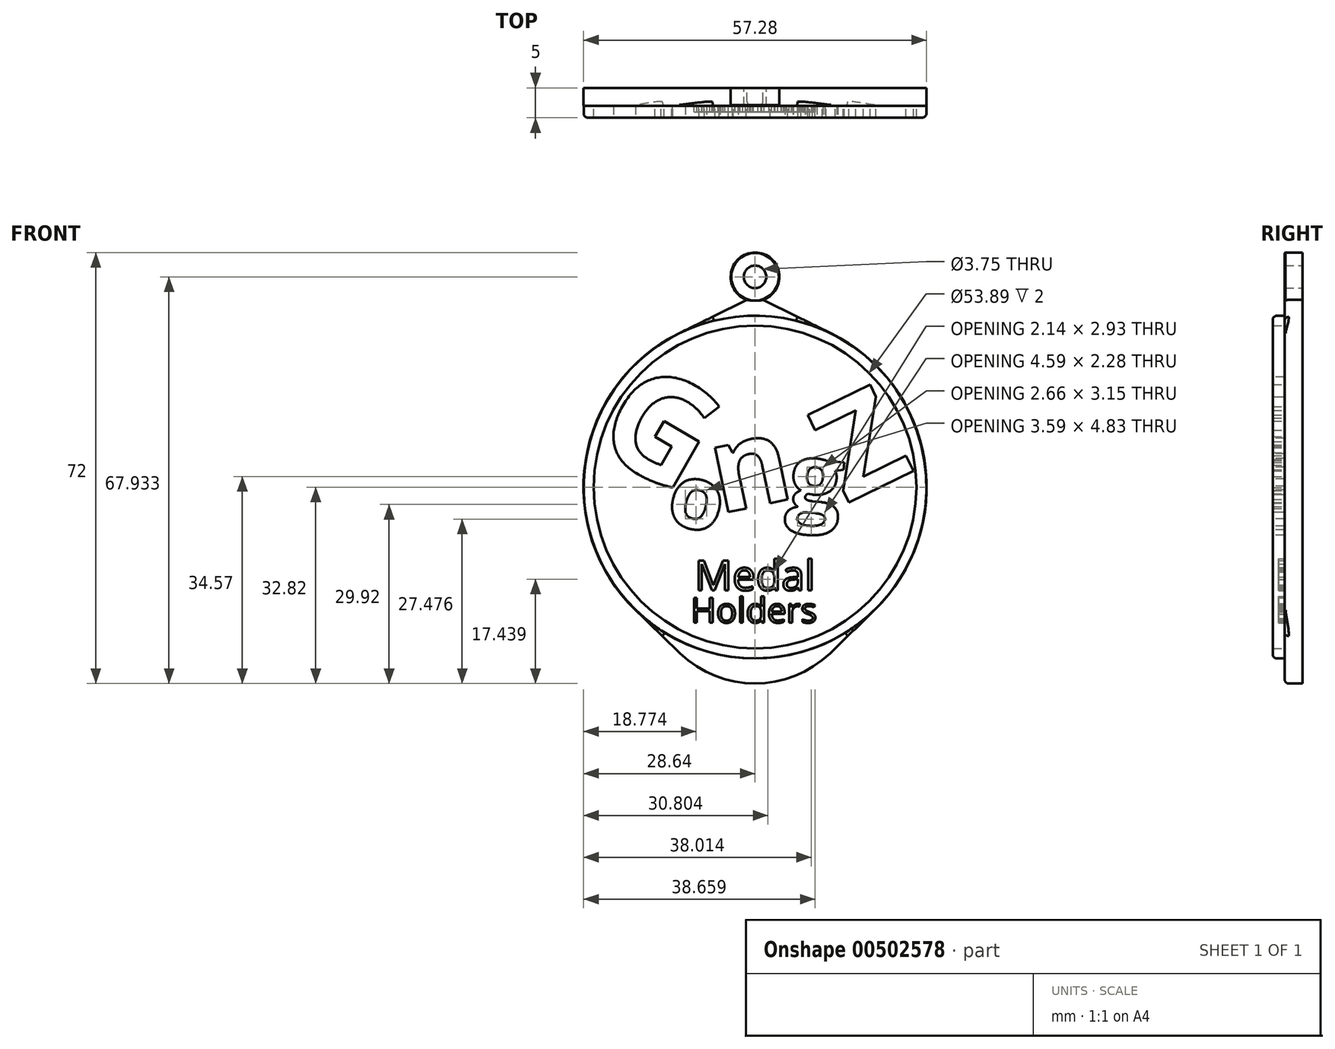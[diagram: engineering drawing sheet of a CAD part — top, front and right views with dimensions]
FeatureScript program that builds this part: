
annotation { "Feature Type Name" : "Feature", "Feature Type Description" : "" }
export const myFeature = defineFeature(function(context is Context, id is Id, definition is map)
    precondition{}
    {
        {
            var Q0;
            Q0=qCreatedBy(makeId("Front.planeOp"),FACE);
            var sketch = newSketch(context, id + "F0", { "sketchPlane" : qUnion([Q0])});
            skArc(sketch, "E0", {"start": v(19.93, -20.57) * mm, "mid": v(28.3, 4.45) * mm, "end": v(12.66, 25.7) * mm});
            skLineSegment(sketch, "E1", {"start": v(-12.53, -27.75) * mm, "end": v(-19.93, -20.57) * mm});
            skLineSegment(sketch, "E2", {"start": v(12.53, -27.75) * mm, "end": v(19.93, -20.57) * mm});
            skPoint(sketch, "E3.visualSharp", {"position": v(0, -39.89) * mm});
            skArc(sketch, "E3.filletArc", {"start": v(-12.53, -27.75) * mm, "mid": v(0, -32.82) * mm, "end": v(12.53, -27.75) * mm});
            skLineSegment(sketch, "E4", {"start": v(-1.34, 31.27) * mm, "end": v(-12.66, 25.7) * mm});
            skLineSegment(sketch, "E5", {"start": v(-12.66, 25.7) * mm, "end": v(-1.34, 31.27) * mm});
            skLineSegment(sketch, "E6", {"start": v(1.34, 31.27) * mm, "end": v(12.66, 25.7) * mm});
            skArc(sketch, "E7.trimOffspring", {"start": v(-12.66, 25.7) * mm, "mid": v(-28.3, 4.45) * mm, "end": v(-19.93, -20.57) * mm});
            skCircle(sketch, "E8", {"center": v(0, 35.11) * mm, "radius": 4.07 * mm});
            skCircle(sketch, "E9", {"center": v(0, 35.11) * mm, "radius": 1.87 * mm});
            skPoint(sketch, "E10.orphan", {"position": v(0, 31.93) * mm});
            skSolve(sketch);
        }
        {
            var Q0;
            Q0 = qSketchRegion(id + "F0", true);
            extrude(context, id + "F1", {"entities" : qUnion([Q0]), "depth" : 3 * mm, "offsetDistance" : 25 * mm});
        }
        {
            var Q0;
            Q0=makeQuery(id+"F1.opExtrude","CAP_FACE",FACE,{"disambiguationData":[OSD([sQuery(id+"F0.wireOp",EDGE,"E0"),sQuery(id+"F0.wireOp",EDGE,"E1"),sQuery(id+"F0.wireOp",EDGE,"E2"),sQuery(id+"F0.wireOp",EDGE,"E3.filletArc"),sQuery(id+"F0.wireOp",EDGE,"E5"),sQuery(id+"F0.wireOp",EDGE,"E6"),sQuery(id+"F0.wireOp",EDGE,"E7.trimOffspring"),sQuery(id+"F0.wireOp",EDGE,"E8"),sQuery(id+"F0.wireOp",EDGE,"E9")])],"isStart":false});
            var sketch = newSketch(context, id + "F2", { "sketchPlane" : qUnion([Q0])});
            skCircle(sketch, "E11", {"center": v(0, 0) * mm, "radius": 28.62 * mm});
            skCircle(sketch, "E12", {"center": v(0, 0) * mm, "radius": 26.95 * mm});
            skSolve(sketch);
        }
        {
            var Q0;
            Q0 = qSketchRegion(id + "F2", true);
            extrude(context, id + "F3", {"entities" : qUnion([Q0]), "operationType" : NewBodyOperationType.ADD, "depth" : 2 * mm, "offsetDistance" : 25 * mm});
        }
        {
            var Q0;
            Q0=makeQuery(id+"F1.opExtrude","CAP_EDGE",EDGE,{"disambiguationData":[OSD([sQuery(id+"F0.wireOp",EDGE,"E3.filletArc")])],"isStart":false});
            var Q1;
            Q1=makeQuery(id+"F1.opExtrude","CAP_EDGE",EDGE,{"disambiguationData":[OSD([sQuery(id+"F0.wireOp",EDGE,"E2")])],"isStart":false});
            var Q2;
            Q2=makeQuery(id+"F1.opExtrude","CAP_EDGE",EDGE,{"disambiguationData":[OSD([sQuery(id+"F0.wireOp",EDGE,"E1")])],"isStart":false});
            var Q3;
            Q3=makeQuery(id+"F3.opExtrude","CAP_EDGE",EDGE,{"disambiguationData":[OSD([sQuery(id+"F2.wireOp",EDGE,"E11")])],"isStart":false});
            fillet(context, id + "F4", {"entities" : qUnion([Q0, Q1, Q2, Q3]), "radius" : .7 * mm, "tangentPropagation" : true, "allowEdgeOverflow" : false});
        }
        {
            var Q0;
            Q0=makeQuery(id+"F1.opExtrude","CAP_EDGE",EDGE,{"disambiguationData":[OSD([sQuery(id+"F0.wireOp",EDGE,"E8")])],"isStart":false});
            chamfer(context, id + "F5", {"entities" : qUnion([Q0]), "width" : .1 * mm, "tangentPropagation" : true});
        }
        {
            var Q0;
            Q0=makeQuery(id+"F3.boolean.opBoolean","SPLIT",FACE,{"disambiguationData":[TD([makeQuery(id+"F3.opExtrude","SWEPT_FACE",FACE,{"disambiguationData":[OSD([sQuery(id+"F2.wireOp",EDGE,"E12")])]})])],"derivedFrom":makeQuery(id+"F1.opExtrude","CAP_FACE",FACE,{"disambiguationData":[OSD([sQuery(id+"F0.wireOp",EDGE,"E0"),sQuery(id+"F0.wireOp",EDGE,"E1"),sQuery(id+"F0.wireOp",EDGE,"E2"),sQuery(id+"F0.wireOp",EDGE,"E3.filletArc"),sQuery(id+"F0.wireOp",EDGE,"E5"),sQuery(id+"F0.wireOp",EDGE,"E6"),sQuery(id+"F0.wireOp",EDGE,"E7.trimOffspring"),sQuery(id+"F0.wireOp",EDGE,"E8"),sQuery(id+"F0.wireOp",EDGE,"E9")])],"isStart":false})});
            var sketch = newSketch(context, id + "F6", { "sketchPlane" : qUnion([Q0])});
            skText(sketch, "E13", { "text": "G", "fontName": "OpenSans-Bold.ttf"});
            const initialGuessF6  = {"E13": [-0.01287, -0.00489, 1, 0, 0.01727]};
            skSetInitialGuess(sketch, initialGuessF6);
            skSolve(sketch);
        }
        {
            var Q0;
            Q0 = qSketchRegion(id + "F6", true);
            extrude(context, id + "F7", {"entities" : qUnion([Q0]), "depth" : 2 * mm, "offsetDistance" : 25 * mm});
        }
        {
            var Q0;
            Q0=makeQuery(id+"F7.opExtrude","SWEPT_BODY",BODY,{"disambiguationData":[OSD([sQuery(id+"F6.wireOp",EDGE,"E13.sketch_text.stroke-0"),sQuery(id+"F6.wireOp",EDGE,"E13.sketch_text.stroke-1"),sQuery(id+"F6.wireOp",EDGE,"E13.sketch_text.stroke-2"),sQuery(id+"F6.wireOp",EDGE,"E13.sketch_text.stroke-3"),sQuery(id+"F6.wireOp",EDGE,"E13.sketch_text.stroke-4"),sQuery(id+"F6.wireOp",EDGE,"E13.sketch_text.stroke-5"),sQuery(id+"F6.wireOp",EDGE,"E13.sketch_text.stroke-6"),sQuery(id+"F6.wireOp",EDGE,"E13.sketch_text.stroke-7"),sQuery(id+"F6.wireOp",EDGE,"E13.sketch_text.stroke-8"),sQuery(id+"F6.wireOp",EDGE,"E13.sketch_text.stroke-9"),sQuery(id+"F6.wireOp",EDGE,"E13.sketch_text.stroke-10"),sQuery(id+"F6.wireOp",EDGE,"E13.sketch_text.stroke-11"),sQuery(id+"F6.wireOp",EDGE,"E13.sketch_text.stroke-12"),sQuery(id+"F6.wireOp",EDGE,"E13.sketch_text.stroke-13"),sQuery(id+"F6.wireOp",EDGE,"E13.sketch_text.stroke-14"),sQuery(id+"F6.wireOp",EDGE,"E13.sketch_text.stroke-15"),sQuery(id+"F6.wireOp",EDGE,"E13.sketch_text.stroke-16"),sQuery(id+"F6.wireOp",EDGE,"E13.sketch_text.stroke-17"),sQuery(id+"F6.wireOp",EDGE,"E13.sketch_text.stroke-18")])]});
            transform(context, id + "F8", {"entities" : qUnion([Q0]), "transformType" : TransformType.TRANSLATION_3D, "dx" : -11.7 * mm, "dy" : 0 * mm, "dz" : 4.6 * mm, "makeCopy" : false});
        }
        {
            var Q0;
            Q0=makeQuery(id+"F7.opExtrude","SWEPT_BODY",BODY,{"disambiguationData":[OSD([sQuery(id+"F6.wireOp",EDGE,"E13.sketch_text.stroke-0"),sQuery(id+"F6.wireOp",EDGE,"E13.sketch_text.stroke-1"),sQuery(id+"F6.wireOp",EDGE,"E13.sketch_text.stroke-2"),sQuery(id+"F6.wireOp",EDGE,"E13.sketch_text.stroke-3"),sQuery(id+"F6.wireOp",EDGE,"E13.sketch_text.stroke-4"),sQuery(id+"F6.wireOp",EDGE,"E13.sketch_text.stroke-5"),sQuery(id+"F6.wireOp",EDGE,"E13.sketch_text.stroke-6"),sQuery(id+"F6.wireOp",EDGE,"E13.sketch_text.stroke-7"),sQuery(id+"F6.wireOp",EDGE,"E13.sketch_text.stroke-8"),sQuery(id+"F6.wireOp",EDGE,"E13.sketch_text.stroke-9"),sQuery(id+"F6.wireOp",EDGE,"E13.sketch_text.stroke-10"),sQuery(id+"F6.wireOp",EDGE,"E13.sketch_text.stroke-11"),sQuery(id+"F6.wireOp",EDGE,"E13.sketch_text.stroke-12"),sQuery(id+"F6.wireOp",EDGE,"E13.sketch_text.stroke-13"),sQuery(id+"F6.wireOp",EDGE,"E13.sketch_text.stroke-14"),sQuery(id+"F6.wireOp",EDGE,"E13.sketch_text.stroke-15"),sQuery(id+"F6.wireOp",EDGE,"E13.sketch_text.stroke-16"),sQuery(id+"F6.wireOp",EDGE,"E13.sketch_text.stroke-17"),sQuery(id+"F6.wireOp",EDGE,"E13.sketch_text.stroke-18")])]});
            var Q1;
            Q1=makeQuery(id+"F7.opExtrude","SWEPT_EDGE",EDGE,{"disambiguationData":[OSD([sQuery(id+"F6.wireOp",EDGE,"E13.sketch_text.stroke-17"),sQuery(id+"F6.wireOp",EDGE,"E13.sketch_text.stroke-18")])]});
            transform(context, id + "F9", {"entities" : qUnion([Q0]), "transformType" : TransformType.ROTATION, "transformAxis" : qUnion([Q1]), "angle" : 30 * degree, "makeCopy" : false});
        }
        {
            var Q0;
            Q0=makeQuery(id+"F7.opExtrude","SWEPT_BODY",BODY,{"disambiguationData":[OSD([sQuery(id+"F6.wireOp",EDGE,"E13.sketch_text.stroke-0"),sQuery(id+"F6.wireOp",EDGE,"E13.sketch_text.stroke-1"),sQuery(id+"F6.wireOp",EDGE,"E13.sketch_text.stroke-2"),sQuery(id+"F6.wireOp",EDGE,"E13.sketch_text.stroke-3"),sQuery(id+"F6.wireOp",EDGE,"E13.sketch_text.stroke-4"),sQuery(id+"F6.wireOp",EDGE,"E13.sketch_text.stroke-5"),sQuery(id+"F6.wireOp",EDGE,"E13.sketch_text.stroke-6"),sQuery(id+"F6.wireOp",EDGE,"E13.sketch_text.stroke-7"),sQuery(id+"F6.wireOp",EDGE,"E13.sketch_text.stroke-8"),sQuery(id+"F6.wireOp",EDGE,"E13.sketch_text.stroke-9"),sQuery(id+"F6.wireOp",EDGE,"E13.sketch_text.stroke-10"),sQuery(id+"F6.wireOp",EDGE,"E13.sketch_text.stroke-11"),sQuery(id+"F6.wireOp",EDGE,"E13.sketch_text.stroke-12"),sQuery(id+"F6.wireOp",EDGE,"E13.sketch_text.stroke-13"),sQuery(id+"F6.wireOp",EDGE,"E13.sketch_text.stroke-14"),sQuery(id+"F6.wireOp",EDGE,"E13.sketch_text.stroke-15"),sQuery(id+"F6.wireOp",EDGE,"E13.sketch_text.stroke-16"),sQuery(id+"F6.wireOp",EDGE,"E13.sketch_text.stroke-17"),sQuery(id+"F6.wireOp",EDGE,"E13.sketch_text.stroke-18")])]});
            transform(context, id + "F10", {"entities" : qUnion([Q0]), "transformType" : TransformType.TRANSLATION_3D, "dx" : -0.8 * mm, "dy" : 0 * mm, "dz" : 2.1 * mm, "makeCopy" : false});
        }
        {
            var Q0;
            Q0=makeQuery(id+"F3.boolean.opBoolean","SPLIT",FACE,{"disambiguationData":[TD([makeQuery(id+"F3.opExtrude","SWEPT_FACE",FACE,{"disambiguationData":[OSD([sQuery(id+"F2.wireOp",EDGE,"E12")])]})])],"derivedFrom":makeQuery(id+"F1.opExtrude","CAP_FACE",FACE,{"disambiguationData":[OSD([sQuery(id+"F0.wireOp",EDGE,"E0"),sQuery(id+"F0.wireOp",EDGE,"E1"),sQuery(id+"F0.wireOp",EDGE,"E2"),sQuery(id+"F0.wireOp",EDGE,"E3.filletArc"),sQuery(id+"F0.wireOp",EDGE,"E5"),sQuery(id+"F0.wireOp",EDGE,"E6"),sQuery(id+"F0.wireOp",EDGE,"E7.trimOffspring"),sQuery(id+"F0.wireOp",EDGE,"E8"),sQuery(id+"F0.wireOp",EDGE,"E9")])],"isStart":false})});
            var sketch = newSketch(context, id + "F11", { "sketchPlane" : qUnion([Q0])});
            skText(sketch, "E14", { "text": "o", "fontName": "OpenSans-Bold.ttf"});
            const initialGuessF11  = {"E14": [-0.00372, -0.00779, 1, 0, 0.0107]};
            skSetInitialGuess(sketch, initialGuessF11);
            skSolve(sketch);
        }
        {
            var Q0;
            Q0 = qSketchRegion(id + "F11", true);
            extrude(context, id + "F12", {"entities" : qUnion([Q0]), "depth" : 2 * mm, "offsetDistance" : 25 * mm});
        }
        {
            var Q0;
            Q0=makeQuery(id+"F12.opExtrude","SWEPT_BODY",BODY,{"disambiguationData":[OSD([sQuery(id+"F11.wireOp",EDGE,"E14.sketch_text.stroke-0"),sQuery(id+"F11.wireOp",EDGE,"E14.sketch_text.stroke-1"),sQuery(id+"F11.wireOp",EDGE,"E14.sketch_text.stroke-2"),sQuery(id+"F11.wireOp",EDGE,"E14.sketch_text.stroke-3"),sQuery(id+"F11.wireOp",EDGE,"E14.sketch_text.stroke-4"),sQuery(id+"F11.wireOp",EDGE,"E14.sketch_text.stroke-5"),sQuery(id+"F11.wireOp",EDGE,"E14.sketch_text.stroke-6"),sQuery(id+"F11.wireOp",EDGE,"E14.sketch_text.stroke-7"),sQuery(id+"F11.wireOp",EDGE,"E14.sketch_text.stroke-8"),sQuery(id+"F11.wireOp",EDGE,"E14.sketch_text.stroke-9"),sQuery(id+"F11.wireOp",EDGE,"E14.sketch_text.stroke-10"),sQuery(id+"F11.wireOp",EDGE,"E14.sketch_text.stroke-11"),sQuery(id+"F11.wireOp",EDGE,"E14.sketch_text.stroke-12"),sQuery(id+"F11.wireOp",EDGE,"E14.sketch_text.stroke-13"),sQuery(id+"F11.wireOp",EDGE,"E14.sketch_text.stroke-14"),sQuery(id+"F11.wireOp",EDGE,"E14.sketch_text.stroke-15"),sQuery(id+"F11.wireOp",EDGE,"E14.sketch_text.stroke-16"),sQuery(id+"F11.wireOp",EDGE,"E14.sketch_text.stroke-17")])]});
            var Q1;
            Q1=makeQuery(id+"F12.opExtrude","SWEPT_EDGE",EDGE,{"disambiguationData":[OSD([sQuery(id+"F11.wireOp",EDGE,"E14.sketch_text.stroke-3"),sQuery(id+"F11.wireOp",EDGE,"E14.sketch_text.stroke-4")])]});
            transform(context, id + "F13", {"entities" : qUnion([Q0]), "transformType" : TransformType.ROTATION, "transformAxis" : qUnion([Q1]), "angle" : 15 * degree, "makeCopy" : false});
        }
        {
            var Q0;
            Q0=makeQuery(id+"F12.opExtrude","SWEPT_BODY",BODY,{"disambiguationData":[OSD([sQuery(id+"F11.wireOp",EDGE,"E14.sketch_text.stroke-0"),sQuery(id+"F11.wireOp",EDGE,"E14.sketch_text.stroke-1"),sQuery(id+"F11.wireOp",EDGE,"E14.sketch_text.stroke-2"),sQuery(id+"F11.wireOp",EDGE,"E14.sketch_text.stroke-3"),sQuery(id+"F11.wireOp",EDGE,"E14.sketch_text.stroke-4"),sQuery(id+"F11.wireOp",EDGE,"E14.sketch_text.stroke-5"),sQuery(id+"F11.wireOp",EDGE,"E14.sketch_text.stroke-6"),sQuery(id+"F11.wireOp",EDGE,"E14.sketch_text.stroke-7"),sQuery(id+"F11.wireOp",EDGE,"E14.sketch_text.stroke-8"),sQuery(id+"F11.wireOp",EDGE,"E14.sketch_text.stroke-9"),sQuery(id+"F11.wireOp",EDGE,"E14.sketch_text.stroke-10"),sQuery(id+"F11.wireOp",EDGE,"E14.sketch_text.stroke-11"),sQuery(id+"F11.wireOp",EDGE,"E14.sketch_text.stroke-12"),sQuery(id+"F11.wireOp",EDGE,"E14.sketch_text.stroke-13"),sQuery(id+"F11.wireOp",EDGE,"E14.sketch_text.stroke-14"),sQuery(id+"F11.wireOp",EDGE,"E14.sketch_text.stroke-15"),sQuery(id+"F11.wireOp",EDGE,"E14.sketch_text.stroke-16"),sQuery(id+"F11.wireOp",EDGE,"E14.sketch_text.stroke-17")])]});
            var Q1;
            Q1=makeQuery(id+"F12.opExtrude","CAP_VERTEX",VERTEX,{"disambiguationData":[OSD([sQuery(id+"F11.wireOp",EDGE,"E14.sketch_text.stroke-3"),sQuery(id+"F11.wireOp",EDGE,"E14.sketch_text.stroke-4")])],"isStart":false});
            transform(context, id + "F14", {"entities" : qUnion([Q0]), "transformType" : TransformType.TRANSLATION_3D, "dx" : -10.8 * mm, "dy" : 0 * mm, "dz" : 0.4 * mm, "makeCopy" : false});
        }
        {
            var Q0;
            Q0=makeQuery(id+"F3.boolean.opBoolean","SPLIT",FACE,{"disambiguationData":[TD([makeQuery(id+"F3.opExtrude","SWEPT_FACE",FACE,{"disambiguationData":[OSD([sQuery(id+"F2.wireOp",EDGE,"E12")])]})])],"derivedFrom":makeQuery(id+"F1.opExtrude","CAP_FACE",FACE,{"disambiguationData":[OSD([sQuery(id+"F0.wireOp",EDGE,"E0"),sQuery(id+"F0.wireOp",EDGE,"E1"),sQuery(id+"F0.wireOp",EDGE,"E2"),sQuery(id+"F0.wireOp",EDGE,"E3.filletArc"),sQuery(id+"F0.wireOp",EDGE,"E5"),sQuery(id+"F0.wireOp",EDGE,"E6"),sQuery(id+"F0.wireOp",EDGE,"E7.trimOffspring"),sQuery(id+"F0.wireOp",EDGE,"E8"),sQuery(id+"F0.wireOp",EDGE,"E9")])],"isStart":false})});
            var sketch = newSketch(context, id + "F15", { "sketchPlane" : qUnion([Q0])});
            skText(sketch, "E15", { "text": "n", "fontName": "OpenSans-Bold.ttf"});
            const initialGuessF15  = {"E15": [0.00514, -0.0092, 1, 0, 0.01447]};
            skSetInitialGuess(sketch, initialGuessF15);
            skSolve(sketch);
        }
        {
            var Q0;
            Q0 = qSketchRegion(id + "F15", true);
            extrude(context, id + "F16", {"entities" : qUnion([Q0]), "depth" : 2 * mm, "offsetDistance" : 25 * mm});
        }
        {
            var Q0;
            Q0=makeQuery(id+"F16.opExtrude","SWEPT_BODY",BODY,{"disambiguationData":[OSD([sQuery(id+"F15.wireOp",EDGE,"E15.sketch_text.stroke-0"),sQuery(id+"F15.wireOp",EDGE,"E15.sketch_text.stroke-1"),sQuery(id+"F15.wireOp",EDGE,"E15.sketch_text.stroke-2"),sQuery(id+"F15.wireOp",EDGE,"E15.sketch_text.stroke-3"),sQuery(id+"F15.wireOp",EDGE,"E15.sketch_text.stroke-4"),sQuery(id+"F15.wireOp",EDGE,"E15.sketch_text.stroke-5"),sQuery(id+"F15.wireOp",EDGE,"E15.sketch_text.stroke-6"),sQuery(id+"F15.wireOp",EDGE,"E15.sketch_text.stroke-7"),sQuery(id+"F15.wireOp",EDGE,"E15.sketch_text.stroke-8"),sQuery(id+"F15.wireOp",EDGE,"E15.sketch_text.stroke-9"),sQuery(id+"F15.wireOp",EDGE,"E15.sketch_text.stroke-10"),sQuery(id+"F15.wireOp",EDGE,"E15.sketch_text.stroke-11"),sQuery(id+"F15.wireOp",EDGE,"E15.sketch_text.stroke-12"),sQuery(id+"F15.wireOp",EDGE,"E15.sketch_text.stroke-13"),sQuery(id+"F15.wireOp",EDGE,"E15.sketch_text.stroke-14"),sQuery(id+"F15.wireOp",EDGE,"E15.sketch_text.stroke-15"),sQuery(id+"F15.wireOp",EDGE,"E15.sketch_text.stroke-16")])]});
            var Q1;
            Q1=makeQuery(id+"F16.opExtrude","SWEPT_EDGE",EDGE,{"disambiguationData":[OSD([sQuery(id+"F15.wireOp",EDGE,"E15.sketch_text.stroke-0"),sQuery(id+"F15.wireOp",EDGE,"E15.sketch_text.stroke-1")])]});
            transform(context, id + "F17", {"entities" : qUnion([Q0]), "transformType" : TransformType.ROTATION, "transformAxis" : qUnion([Q1]), "angle" : 12 * degree, "oppositeDirection" : true, "makeCopy" : false});
        }
        {
            var Q0;
            Q0=makeQuery(id+"F16.opExtrude","SWEPT_BODY",BODY,{"disambiguationData":[OSD([sQuery(id+"F15.wireOp",EDGE,"E15.sketch_text.stroke-0"),sQuery(id+"F15.wireOp",EDGE,"E15.sketch_text.stroke-1"),sQuery(id+"F15.wireOp",EDGE,"E15.sketch_text.stroke-2"),sQuery(id+"F15.wireOp",EDGE,"E15.sketch_text.stroke-3"),sQuery(id+"F15.wireOp",EDGE,"E15.sketch_text.stroke-4"),sQuery(id+"F15.wireOp",EDGE,"E15.sketch_text.stroke-5"),sQuery(id+"F15.wireOp",EDGE,"E15.sketch_text.stroke-6"),sQuery(id+"F15.wireOp",EDGE,"E15.sketch_text.stroke-7"),sQuery(id+"F15.wireOp",EDGE,"E15.sketch_text.stroke-8"),sQuery(id+"F15.wireOp",EDGE,"E15.sketch_text.stroke-9"),sQuery(id+"F15.wireOp",EDGE,"E15.sketch_text.stroke-10"),sQuery(id+"F15.wireOp",EDGE,"E15.sketch_text.stroke-11"),sQuery(id+"F15.wireOp",EDGE,"E15.sketch_text.stroke-12"),sQuery(id+"F15.wireOp",EDGE,"E15.sketch_text.stroke-13"),sQuery(id+"F15.wireOp",EDGE,"E15.sketch_text.stroke-14"),sQuery(id+"F15.wireOp",EDGE,"E15.sketch_text.stroke-15"),sQuery(id+"F15.wireOp",EDGE,"E15.sketch_text.stroke-16")])]});
            transform(context, id + "F18", {"entities" : qUnion([Q0]), "transformType" : TransformType.TRANSLATION_3D, "dx" : -11.3 * mm, "dy" : 0 * mm, "dz" : 6.5 * mm, "makeCopy" : false});
        }
        {
            var Q0;
            Q0=makeQuery(id+"F3.boolean.opBoolean","SPLIT",FACE,{"disambiguationData":[TD([makeQuery(id+"F3.opExtrude","SWEPT_FACE",FACE,{"disambiguationData":[OSD([sQuery(id+"F2.wireOp",EDGE,"E12")])]})])],"derivedFrom":makeQuery(id+"F1.opExtrude","CAP_FACE",FACE,{"disambiguationData":[OSD([sQuery(id+"F0.wireOp",EDGE,"E0"),sQuery(id+"F0.wireOp",EDGE,"E1"),sQuery(id+"F0.wireOp",EDGE,"E2"),sQuery(id+"F0.wireOp",EDGE,"E3.filletArc"),sQuery(id+"F0.wireOp",EDGE,"E5"),sQuery(id+"F0.wireOp",EDGE,"E6"),sQuery(id+"F0.wireOp",EDGE,"E7.trimOffspring"),sQuery(id+"F0.wireOp",EDGE,"E8"),sQuery(id+"F0.wireOp",EDGE,"E9")])],"isStart":false})});
            var sketch = newSketch(context, id + "F19", { "sketchPlane" : qUnion([Q0])});
            skText(sketch, "E16", { "text": "g", "fontName": "OpenSans-Bold.ttf"});
            const initialGuessF19  = {"E16": [0.00974, -0.00392, 1, 0, 0.01165]};
            skSetInitialGuess(sketch, initialGuessF19);
            skSolve(sketch);
        }
        {
            var Q0;
            Q0 = qSketchRegion(id + "F19", true);
            extrude(context, id + "F20", {"entities" : qUnion([Q0]), "depth" : 2 * mm, "offsetDistance" : 25 * mm});
        }
        {
            var Q0;
            Q0=makeQuery(id+"F3.boolean.opBoolean","SPLIT",FACE,{"disambiguationData":[TD([makeQuery(id+"F3.opExtrude","SWEPT_FACE",FACE,{"disambiguationData":[OSD([sQuery(id+"F2.wireOp",EDGE,"E12")])]})])],"derivedFrom":makeQuery(id+"F1.opExtrude","CAP_FACE",FACE,{"disambiguationData":[OSD([sQuery(id+"F0.wireOp",EDGE,"E0"),sQuery(id+"F0.wireOp",EDGE,"E1"),sQuery(id+"F0.wireOp",EDGE,"E2"),sQuery(id+"F0.wireOp",EDGE,"E3.filletArc"),sQuery(id+"F0.wireOp",EDGE,"E5"),sQuery(id+"F0.wireOp",EDGE,"E6"),sQuery(id+"F0.wireOp",EDGE,"E7.trimOffspring"),sQuery(id+"F0.wireOp",EDGE,"E8"),sQuery(id+"F0.wireOp",EDGE,"E9")])],"isStart":false})});
            var sketch = newSketch(context, id + "F21", { "sketchPlane" : qUnion([Q0])});
            skText(sketch, "E17", { "text": "Z", "fontName": "OpenSans-Bold.ttf"});
            const initialGuessF21  = {"E17": [0.00874, -0.0082, 1, 0, 0.01626]};
            skSetInitialGuess(sketch, initialGuessF21);
            skSolve(sketch);
        }
        {
            var Q0;
            Q0 = qSketchRegion(id + "F21", true);
            extrude(context, id + "F22", {"entities" : qUnion([Q0]), "depth" : 2 * mm, "offsetDistance" : 25 * mm});
        }
        {
            var Q0;
            Q0=makeQuery(id+"F22.opExtrude","SWEPT_BODY",BODY,{"disambiguationData":[OSD([sQuery(id+"F21.wireOp",EDGE,"E17.sketch_text.stroke-0"),sQuery(id+"F21.wireOp",EDGE,"E17.sketch_text.stroke-1"),sQuery(id+"F21.wireOp",EDGE,"E17.sketch_text.stroke-2"),sQuery(id+"F21.wireOp",EDGE,"E17.sketch_text.stroke-3"),sQuery(id+"F21.wireOp",EDGE,"E17.sketch_text.stroke-4"),sQuery(id+"F21.wireOp",EDGE,"E17.sketch_text.stroke-5"),sQuery(id+"F21.wireOp",EDGE,"E17.sketch_text.stroke-6"),sQuery(id+"F21.wireOp",EDGE,"E17.sketch_text.stroke-7"),sQuery(id+"F21.wireOp",EDGE,"E17.sketch_text.stroke-8"),sQuery(id+"F21.wireOp",EDGE,"E17.sketch_text.stroke-9")])]});
            transform(context, id + "F23", {"entities" : qUnion([Q0]), "transformType" : TransformType.TRANSLATION_3D, "dx" : -0.9 * mm, "dy" : 0 * mm, "dz" : 9.4 * mm, "makeCopy" : false});
        }
        {
            var Q0;
            Q0=makeQuery(id+"F22.opExtrude","SWEPT_BODY",BODY,{"disambiguationData":[OSD([sQuery(id+"F21.wireOp",EDGE,"E17.sketch_text.stroke-0"),sQuery(id+"F21.wireOp",EDGE,"E17.sketch_text.stroke-1"),sQuery(id+"F21.wireOp",EDGE,"E17.sketch_text.stroke-2"),sQuery(id+"F21.wireOp",EDGE,"E17.sketch_text.stroke-3"),sQuery(id+"F21.wireOp",EDGE,"E17.sketch_text.stroke-4"),sQuery(id+"F21.wireOp",EDGE,"E17.sketch_text.stroke-5"),sQuery(id+"F21.wireOp",EDGE,"E17.sketch_text.stroke-6"),sQuery(id+"F21.wireOp",EDGE,"E17.sketch_text.stroke-7"),sQuery(id+"F21.wireOp",EDGE,"E17.sketch_text.stroke-8"),sQuery(id+"F21.wireOp",EDGE,"E17.sketch_text.stroke-9")])]});
            var Q1;
            Q1=makeQuery(id+"F22.opExtrude","SWEPT_EDGE",EDGE,{"disambiguationData":[OSD([sQuery(id+"F21.wireOp",EDGE,"E17.sketch_text.stroke-6"),sQuery(id+"F21.wireOp",EDGE,"E17.sketch_text.stroke-7")])]});
            transform(context, id + "F24", {"entities" : qUnion([Q0]), "transformType" : TransformType.ROTATION, "transformAxis" : qUnion([Q1]), "angle" : 26 * degree, "oppositeDirection" : true, "makeCopy" : false});
        }
        {
            var Q0;
            Q0=makeQuery(id+"F20.opExtrude","SWEPT_BODY",BODY,{"disambiguationData":[OSD([sQuery(id+"F19.wireOp",EDGE,"E16.sketch_text.stroke-0"),sQuery(id+"F19.wireOp",EDGE,"E16.sketch_text.stroke-1"),sQuery(id+"F19.wireOp",EDGE,"E16.sketch_text.stroke-2"),sQuery(id+"F19.wireOp",EDGE,"E16.sketch_text.stroke-3"),sQuery(id+"F19.wireOp",EDGE,"E16.sketch_text.stroke-4"),sQuery(id+"F19.wireOp",EDGE,"E16.sketch_text.stroke-5"),sQuery(id+"F19.wireOp",EDGE,"E16.sketch_text.stroke-6"),sQuery(id+"F19.wireOp",EDGE,"E16.sketch_text.stroke-7"),sQuery(id+"F19.wireOp",EDGE,"E16.sketch_text.stroke-8"),sQuery(id+"F19.wireOp",EDGE,"E16.sketch_text.stroke-9"),sQuery(id+"F19.wireOp",EDGE,"E16.sketch_text.stroke-10"),sQuery(id+"F19.wireOp",EDGE,"E16.sketch_text.stroke-11"),sQuery(id+"F19.wireOp",EDGE,"E16.sketch_text.stroke-12"),sQuery(id+"F19.wireOp",EDGE,"E16.sketch_text.stroke-13"),sQuery(id+"F19.wireOp",EDGE,"E16.sketch_text.stroke-14"),sQuery(id+"F19.wireOp",EDGE,"E16.sketch_text.stroke-15"),sQuery(id+"F19.wireOp",EDGE,"E16.sketch_text.stroke-16"),sQuery(id+"F19.wireOp",EDGE,"E16.sketch_text.stroke-17"),sQuery(id+"F19.wireOp",EDGE,"E16.sketch_text.stroke-18"),sQuery(id+"F19.wireOp",EDGE,"E16.sketch_text.stroke-19"),sQuery(id+"F19.wireOp",EDGE,"E16.sketch_text.stroke-20"),sQuery(id+"F19.wireOp",EDGE,"E16.sketch_text.stroke-21"),sQuery(id+"F19.wireOp",EDGE,"E16.sketch_text.stroke-22"),sQuery(id+"F19.wireOp",EDGE,"E16.sketch_text.stroke-23"),sQuery(id+"F19.wireOp",EDGE,"E16.sketch_text.stroke-24"),sQuery(id+"F19.wireOp",EDGE,"E16.sketch_text.stroke-25"),sQuery(id+"F19.wireOp",EDGE,"E16.sketch_text.stroke-26"),sQuery(id+"F19.wireOp",EDGE,"E16.sketch_text.stroke-27"),sQuery(id+"F19.wireOp",EDGE,"E16.sketch_text.stroke-28"),sQuery(id+"F19.wireOp",EDGE,"E16.sketch_text.stroke-29"),sQuery(id+"F19.wireOp",EDGE,"E16.sketch_text.stroke-30"),sQuery(id+"F19.wireOp",EDGE,"E16.sketch_text.stroke-31"),sQuery(id+"F19.wireOp",EDGE,"E16.sketch_text.stroke-32"),sQuery(id+"F19.wireOp",EDGE,"E16.sketch_text.stroke-33"),sQuery(id+"F19.wireOp",EDGE,"E16.sketch_text.stroke-34"),sQuery(id+"F19.wireOp",EDGE,"E16.sketch_text.stroke-35"),sQuery(id+"F19.wireOp",EDGE,"E16.sketch_text.stroke-36"),sQuery(id+"F19.wireOp",EDGE,"E16.sketch_text.stroke-37"),sQuery(id+"F19.wireOp",EDGE,"E16.sketch_text.stroke-38"),sQuery(id+"F19.wireOp",EDGE,"E16.sketch_text.stroke-39"),sQuery(id+"F19.wireOp",EDGE,"E16.sketch_text.stroke-40"),sQuery(id+"F19.wireOp",EDGE,"E16.sketch_text.stroke-41"),sQuery(id+"F19.wireOp",EDGE,"E16.sketch_text.stroke-42"),sQuery(id+"F19.wireOp",EDGE,"E16.sketch_text.stroke-43")])]});
            var Q1;
            Q1=makeQuery(id+"F20.opExtrude","CAP_VERTEX",VERTEX,{"disambiguationData":[OSD([sQuery(id+"F19.wireOp",EDGE,"E16.sketch_text.stroke-15"),sQuery(id+"F19.wireOp",EDGE,"E16.sketch_text.stroke-16")])],"isStart":false});
            var Q2;
            Q2=makeQuery(id+"F20.opExtrude","SWEPT_EDGE",EDGE,{"disambiguationData":[OSD([sQuery(id+"F19.wireOp",EDGE,"E16.sketch_text.stroke-15"),sQuery(id+"F19.wireOp",EDGE,"E16.sketch_text.stroke-16")])]});
            transform(context, id + "F25", {"entities" : qUnion([Q0]), "transformType" : TransformType.ROTATION, "transformAxis" : qUnion([Q2]), "angle" : 6 * degree, "makeCopy" : false});
        }
        {
            var Q0;
            Q0=makeQuery(id+"F20.opExtrude","SWEPT_BODY",BODY,{"disambiguationData":[OSD([sQuery(id+"F19.wireOp",EDGE,"E16.sketch_text.stroke-0"),sQuery(id+"F19.wireOp",EDGE,"E16.sketch_text.stroke-1"),sQuery(id+"F19.wireOp",EDGE,"E16.sketch_text.stroke-2"),sQuery(id+"F19.wireOp",EDGE,"E16.sketch_text.stroke-3"),sQuery(id+"F19.wireOp",EDGE,"E16.sketch_text.stroke-4"),sQuery(id+"F19.wireOp",EDGE,"E16.sketch_text.stroke-5"),sQuery(id+"F19.wireOp",EDGE,"E16.sketch_text.stroke-6"),sQuery(id+"F19.wireOp",EDGE,"E16.sketch_text.stroke-7"),sQuery(id+"F19.wireOp",EDGE,"E16.sketch_text.stroke-8"),sQuery(id+"F19.wireOp",EDGE,"E16.sketch_text.stroke-9"),sQuery(id+"F19.wireOp",EDGE,"E16.sketch_text.stroke-10"),sQuery(id+"F19.wireOp",EDGE,"E16.sketch_text.stroke-11"),sQuery(id+"F19.wireOp",EDGE,"E16.sketch_text.stroke-12"),sQuery(id+"F19.wireOp",EDGE,"E16.sketch_text.stroke-13"),sQuery(id+"F19.wireOp",EDGE,"E16.sketch_text.stroke-14"),sQuery(id+"F19.wireOp",EDGE,"E16.sketch_text.stroke-15"),sQuery(id+"F19.wireOp",EDGE,"E16.sketch_text.stroke-16"),sQuery(id+"F19.wireOp",EDGE,"E16.sketch_text.stroke-17"),sQuery(id+"F19.wireOp",EDGE,"E16.sketch_text.stroke-18"),sQuery(id+"F19.wireOp",EDGE,"E16.sketch_text.stroke-19"),sQuery(id+"F19.wireOp",EDGE,"E16.sketch_text.stroke-20"),sQuery(id+"F19.wireOp",EDGE,"E16.sketch_text.stroke-21"),sQuery(id+"F19.wireOp",EDGE,"E16.sketch_text.stroke-22"),sQuery(id+"F19.wireOp",EDGE,"E16.sketch_text.stroke-23"),sQuery(id+"F19.wireOp",EDGE,"E16.sketch_text.stroke-24"),sQuery(id+"F19.wireOp",EDGE,"E16.sketch_text.stroke-25"),sQuery(id+"F19.wireOp",EDGE,"E16.sketch_text.stroke-26"),sQuery(id+"F19.wireOp",EDGE,"E16.sketch_text.stroke-27"),sQuery(id+"F19.wireOp",EDGE,"E16.sketch_text.stroke-28"),sQuery(id+"F19.wireOp",EDGE,"E16.sketch_text.stroke-29"),sQuery(id+"F19.wireOp",EDGE,"E16.sketch_text.stroke-30"),sQuery(id+"F19.wireOp",EDGE,"E16.sketch_text.stroke-31"),sQuery(id+"F19.wireOp",EDGE,"E16.sketch_text.stroke-32"),sQuery(id+"F19.wireOp",EDGE,"E16.sketch_text.stroke-33"),sQuery(id+"F19.wireOp",EDGE,"E16.sketch_text.stroke-34"),sQuery(id+"F19.wireOp",EDGE,"E16.sketch_text.stroke-35"),sQuery(id+"F19.wireOp",EDGE,"E16.sketch_text.stroke-36"),sQuery(id+"F19.wireOp",EDGE,"E16.sketch_text.stroke-37"),sQuery(id+"F19.wireOp",EDGE,"E16.sketch_text.stroke-38"),sQuery(id+"F19.wireOp",EDGE,"E16.sketch_text.stroke-39"),sQuery(id+"F19.wireOp",EDGE,"E16.sketch_text.stroke-40"),sQuery(id+"F19.wireOp",EDGE,"E16.sketch_text.stroke-41"),sQuery(id+"F19.wireOp",EDGE,"E16.sketch_text.stroke-42"),sQuery(id+"F19.wireOp",EDGE,"E16.sketch_text.stroke-43")])]});
            transform(context, id + "F26", {"entities" : qUnion([Q0]), "transformType" : TransformType.TRANSLATION_3D, "dx" : -4.8 * mm, "dy" : 0 * mm, "dz" : 0.2 * mm, "makeCopy" : false});
        }
        {
            var Q0;
            Q0=makeQuery(id+"F3.boolean.opBoolean","SPLIT",FACE,{"disambiguationData":[TD([makeQuery(id+"F3.opExtrude","SWEPT_FACE",FACE,{"disambiguationData":[OSD([sQuery(id+"F2.wireOp",EDGE,"E12")])]})])],"derivedFrom":makeQuery(id+"F1.opExtrude","CAP_FACE",FACE,{"disambiguationData":[OSD([sQuery(id+"F0.wireOp",EDGE,"E0"),sQuery(id+"F0.wireOp",EDGE,"E1"),sQuery(id+"F0.wireOp",EDGE,"E2"),sQuery(id+"F0.wireOp",EDGE,"E3.filletArc"),sQuery(id+"F0.wireOp",EDGE,"E5"),sQuery(id+"F0.wireOp",EDGE,"E6"),sQuery(id+"F0.wireOp",EDGE,"E7.trimOffspring"),sQuery(id+"F0.wireOp",EDGE,"E8"),sQuery(id+"F0.wireOp",EDGE,"E9")])],"isStart":false})});
            var sketch = newSketch(context, id + "F27", { "sketchPlane" : qUnion([Q0])});
            skText(sketch, "E18", { "text": "Medal", "fontName": "OpenSans-Regular.ttf"});
            skText(sketch, "E19", { "text": "Holders", "fontName": "OpenSans-Regular.ttf"});
            const initialGuessF27  = {"E18": [-0.01011, -0.01725, 1, 0, 0.00503], "E19": [-0.01077, -0.02264, 1, 0, 0.00416]};
            skSetInitialGuess(sketch, initialGuessF27);
            skSolve(sketch);
        }
        {
            var Q0;
            Q0 = qSketchRegion(id + "F27", true);
            extrude(context, id + "F28", {"entities" : qUnion([Q0]), "depth" : 1 * mm, "offsetDistance" : 25 * mm});
        }
    });
